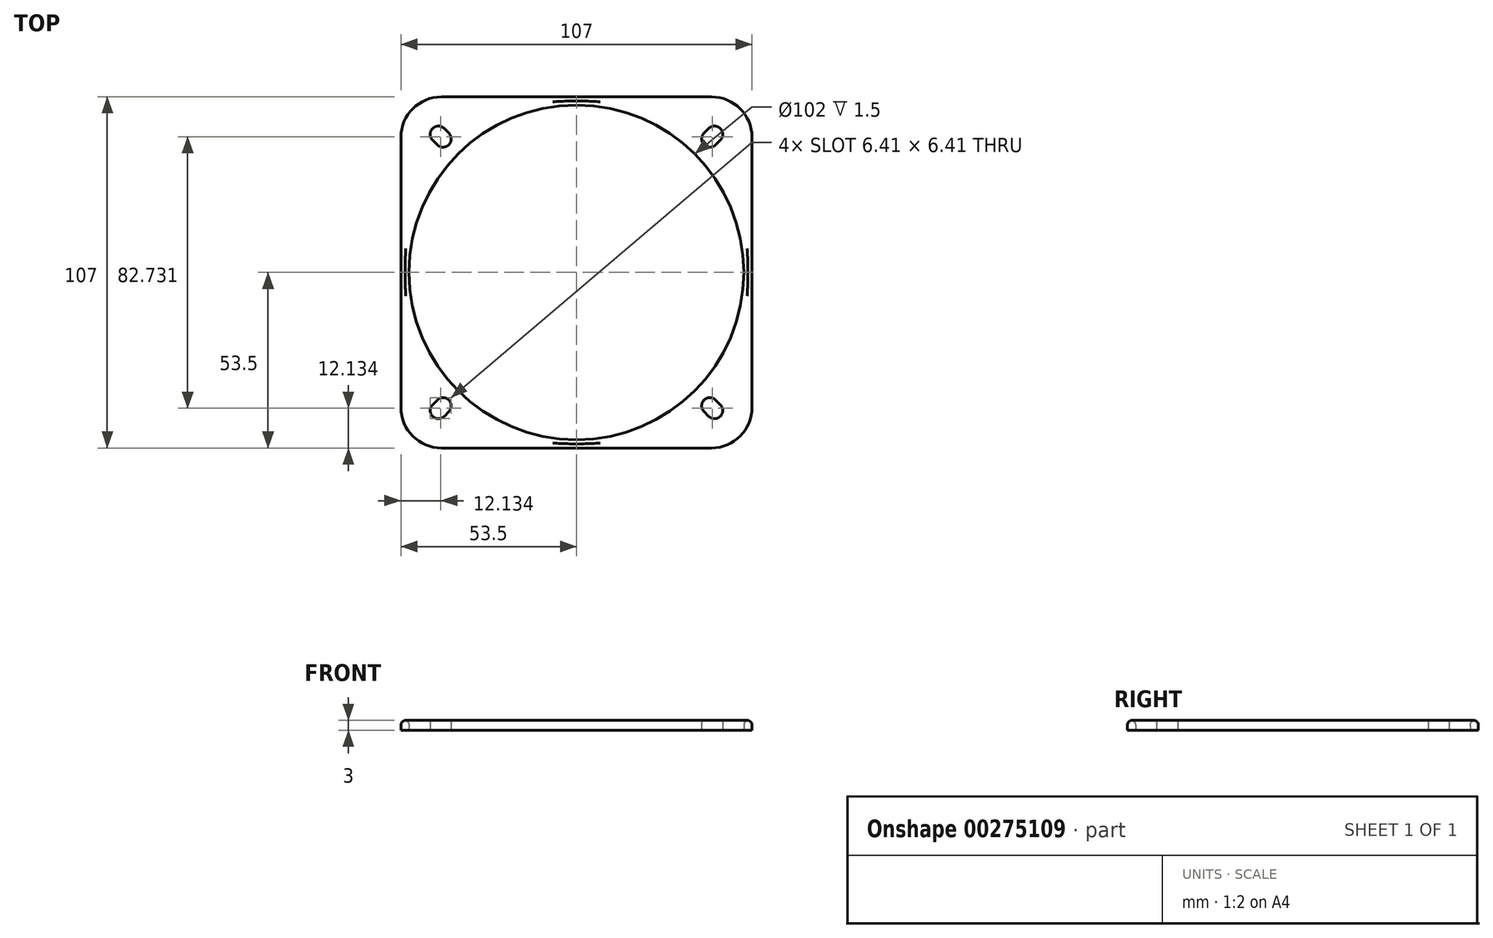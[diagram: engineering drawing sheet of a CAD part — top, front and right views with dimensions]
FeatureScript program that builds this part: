
annotation { "Feature Type Name" : "Feature", "Feature Type Description" : "" }
export const myFeature = defineFeature(function(context is Context, id is Id, definition is map)
    precondition{}
    {
        {
            var Q0;
            Q0=qCreatedBy(makeId("Top.planeOp"),FACE);
            var sketch = newSketch(context, id + "F0", { "sketchPlane" : qUnion([Q0])});
            skCircle(sketch, "E0", {"center": v(0, 0) * mm, "radius": 51 * mm});
            skLineSegment(sketch, "E1.bottom", {"start": v(-41.16, 53.5) * mm, "end": v(41.16, 53.5) * mm});
            skLineSegment(sketch, "E1.top", {"start": v(-41.16, -53.5) * mm, "end": v(41.16, -53.5) * mm});
            skLineSegment(sketch, "E1.left", {"start": v(-53.5, 41.16) * mm, "end": v(-53.5, -41.16) * mm});
            skLineSegment(sketch, "E1.right", {"start": v(53.5, 41.16) * mm, "end": v(53.5, -41.16) * mm});
            skPoint(sketch, "E2.orphan", {"position": v(53.5, 53.5) * mm});
            skPoint(sketch, "E3.orphan", {"position": v(-53.5, 53.5) * mm});
            skPoint(sketch, "E4.orphan", {"position": v(-53.5, -53.5) * mm});
            skPoint(sketch, "E5.orphan", {"position": v(53.5, -53.5) * mm});
            skLineSegment(sketch, "E6", {"start": v(-47.73, 47.73) * mm, "end": v(-36.06, 36.06) * mm, "construction": true});
            skPoint(sketch, "E7", {"position": v(-36.06, 36.06) * mm});
            skPoint(sketch, "E8", {"position": v(-38.9, 38.9) * mm});
            skPoint(sketch, "E9", {"position": v(-43.84, 43.84) * mm});
            skPoint(sketch, "E10", {"position": v(-40.66, 40.66) * mm});
            skPoint(sketch, "E11", {"position": v(-42.07, 42.07) * mm});
            skArc(sketch, "E12", {"start": v(-40.3, 43.84) * mm, "mid": v(-43.84, 43.84) * mm, "end": v(-43.84, 40.3) * mm});
            skArc(sketch, "E13", {"start": v(-42.43, 38.9) * mm, "mid": v(-38.9, 38.9) * mm, "end": v(-38.9, 42.43) * mm});
            skLineSegment(sketch, "E14", {"start": v(-40.3, 43.84) * mm, "end": v(-38.9, 42.43) * mm});
            skLineSegment(sketch, "E15", {"start": v(-43.84, 40.3) * mm, "end": v(-42.43, 38.9) * mm});
            skArc(sketch, "E16", {"start": v(-41.16, 53.5) * mm, "mid": v(-49.89, 49.89) * mm, "end": v(-53.5, 41.16) * mm});
            skArc(sketch, "E17.1.0", {"start": v(-53.5, -41.16) * mm, "mid": v(-49.89, -49.89) * mm, "end": v(-41.16, -53.5) * mm});
            skArc(sketch, "E17.1.1", {"start": v(-43.84, -40.3) * mm, "mid": v(-43.84, -43.84) * mm, "end": v(-40.3, -43.84) * mm});
            skLineSegment(sketch, "E17.1.2", {"start": v(-43.84, -40.3) * mm, "end": v(-42.43, -38.9) * mm});
            skArc(sketch, "E17.1.3", {"start": v(-38.9, -42.43) * mm, "mid": v(-38.9, -38.9) * mm, "end": v(-42.43, -38.9) * mm});
            skLineSegment(sketch, "E17.1.4", {"start": v(-40.3, -43.84) * mm, "end": v(-38.9, -42.43) * mm});
            skArc(sketch, "E17.2.0", {"start": v(41.16, -53.5) * mm, "mid": v(49.89, -49.89) * mm, "end": v(53.5, -41.16) * mm});
            skArc(sketch, "E17.2.1", {"start": v(40.3, -43.84) * mm, "mid": v(43.84, -43.84) * mm, "end": v(43.84, -40.3) * mm});
            skLineSegment(sketch, "E17.2.2", {"start": v(40.3, -43.84) * mm, "end": v(38.9, -42.43) * mm});
            skArc(sketch, "E17.2.3", {"start": v(42.43, -38.9) * mm, "mid": v(38.9, -38.9) * mm, "end": v(38.9, -42.43) * mm});
            skLineSegment(sketch, "E17.2.4", {"start": v(43.84, -40.3) * mm, "end": v(42.43, -38.9) * mm});
            skArc(sketch, "E17.3.0", {"start": v(53.5, 41.16) * mm, "mid": v(49.89, 49.89) * mm, "end": v(41.16, 53.5) * mm});
            skArc(sketch, "E17.3.1", {"start": v(43.84, 40.3) * mm, "mid": v(43.84, 43.84) * mm, "end": v(40.3, 43.84) * mm});
            skLineSegment(sketch, "E17.3.2", {"start": v(43.84, 40.3) * mm, "end": v(42.43, 38.9) * mm});
            skArc(sketch, "E17.3.3", {"start": v(38.9, 42.43) * mm, "mid": v(38.9, 38.9) * mm, "end": v(42.43, 38.9) * mm});
            skLineSegment(sketch, "E17.3.4", {"start": v(40.3, 43.84) * mm, "end": v(38.9, 42.43) * mm});
            skSolve(sketch);
        }
        {
            var Q0;
            Q0=makeQuery(id+"F0.imprint","IMPRINT",FACE,{"disambiguationData":[TD([[makeQuery(id+"F0.imprint","IMPRINT",EDGE,{"derivedFrom":sQuery(id+"F0.wireOp",EDGE,"E0")}),-1.0]])]});
            extrude(context, id + "F1", {"entities" : qUnion([Q0]), "depth" : 3 * mm});
        }
        {
            var Q0;
            Q0=makeQuery(id+"F1.opExtrude","CAP_EDGE",EDGE,{"disambiguationData":[OSD([sQuery(id+"F0.wireOp",EDGE,"E1.left")])],"isStart":false});
            var Q1;
            Q1=makeQuery(id+"F1.opExtrude","CAP_EDGE",EDGE,{"disambiguationData":[OSD([sQuery(id+"F0.wireOp",EDGE,"E16")])],"isStart":false});
            var Q2;
            Q2=makeQuery(id+"F1.opExtrude","CAP_EDGE",EDGE,{"disambiguationData":[OSD([sQuery(id+"F0.wireOp",EDGE,"E1.bottom")])],"isStart":false});
            var Q3;
            Q3=makeQuery(id+"F1.opExtrude","CAP_EDGE",EDGE,{"disambiguationData":[OSD([sQuery(id+"F0.wireOp",EDGE,"E17.3.0")])],"isStart":false});
            var Q4;
            Q4=makeQuery(id+"F1.opExtrude","CAP_EDGE",EDGE,{"disambiguationData":[OSD([sQuery(id+"F0.wireOp",EDGE,"E17.1.0")])],"isStart":false});
            var Q5;
            Q5=makeQuery(id+"F1.opExtrude","CAP_EDGE",EDGE,{"disambiguationData":[OSD([sQuery(id+"F0.wireOp",EDGE,"E1.top")])],"isStart":false});
            var Q6;
            Q6=makeQuery(id+"F1.opExtrude","CAP_EDGE",EDGE,{"disambiguationData":[OSD([sQuery(id+"F0.wireOp",EDGE,"E17.2.0")])],"isStart":false});
            var Q7;
            Q7=makeQuery(id+"F1.opExtrude","CAP_EDGE",EDGE,{"disambiguationData":[OSD([sQuery(id+"F0.wireOp",EDGE,"E0")])],"isStart":false});
            fillet(context, id + "F2", {"entities" : qUnion([Q0, Q1, Q2, Q3, Q4, Q5, Q6, Q7]), "radius" : 1.5 * mm, "tangentPropagation" : true, "allowEdgeOverflow" : false});
        }
    });
